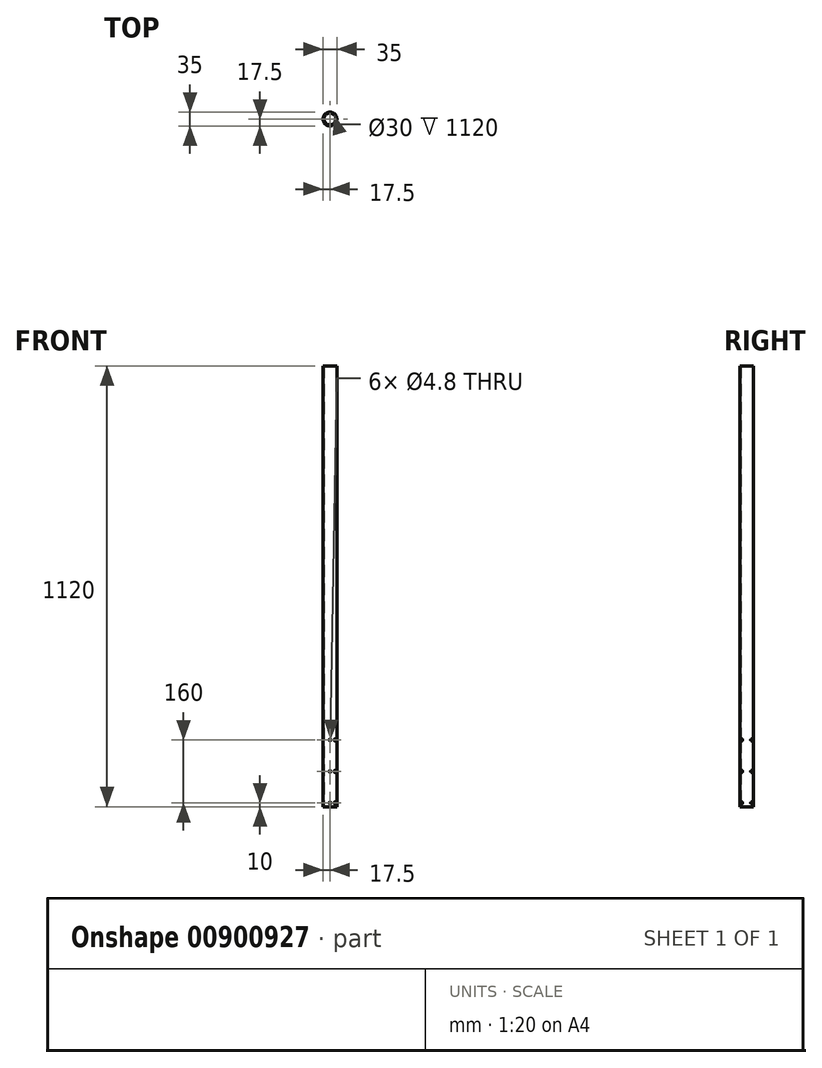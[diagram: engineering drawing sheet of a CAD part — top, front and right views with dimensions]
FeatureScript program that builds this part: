
annotation { "Feature Type Name" : "Feature", "Feature Type Description" : "" }
export const myFeature = defineFeature(function(context is Context, id is Id, definition is map)
    precondition{}
    {
        {
            var Q0;
            Q0=qCreatedBy(makeId("Top.planeOp"),FACE);
            var sketch = newSketch(context, id + "F0", { "sketchPlane" : qUnion([Q0])});
            skCircle(sketch, "E0", {"center": v(0, 0) * mm, "radius": 17.5 * mm});
            skLineSegment(sketch, "E1", {"start": v(0, 17.5) * mm, "end": v(0, -17.5) * mm});
            skSolve(sketch);
        }
        {
            var Q0;
            Q0 = qSketchRegion(id + "F0", true);
            extrude(context, id + "F1", {"entities" : qUnion([Q0]), "depth" : 1120 * mm, "offsetDistance" : 25 * mm});
        }
        {
            var Q0;
            Q0=sQuery(id+"F0.wireOp",VERTEX,"E0.center");
            var Q1;
            Q1=makeQuery(id+"F1.opExtrude","SWEPT_BODY",BODY,{"disambiguationData":[OSD([sQuery(id+"F0.wireOp",EDGE,"E0")])]});
            hole(context, id + "F2", {"style" : HoleStyle.SIMPLE, "endStyle" : HoleEndStyle.THROUGH, "oppositeDirection" : true, "holeDiameter" : 30 * mm, "majorDiameter" : 10 * mm, "isTappedThrough" : true, "tappedDepth" : 12 * mm, "tapClearance" : 3, "locations" : qUnion([Q0]), "scope" : qUnion([Q1])});
        }
        {
            var Q0;
            Q0=qCreatedBy(makeId("Front.planeOp"),FACE);
            var sketch = newSketch(context, id + "F3", { "sketchPlane" : qUnion([Q0])});
            skLineSegment(sketch, "E2.bottom", {"start": v(-17.5, 10) * mm, "end": v(17.5, 10) * mm});
            skLineSegment(sketch, "E2.top", {"start": v(-17.5, -10) * mm, "end": v(17.5, -10) * mm});
            skLineSegment(sketch, "E2.left", {"start": v(-17.5, 10) * mm, "end": v(-17.5, -10) * mm});
            skLineSegment(sketch, "E2.right", {"start": v(17.5, 10) * mm, "end": v(17.5, -10) * mm});
            skPoint(sketch, "E2.middle", {"position": v(0, 0) * mm});
            skLineSegment(sketch, "E3.top", {"start": v(-17.5, 90) * mm, "end": v(17.5, 90) * mm});
            skLineSegment(sketch, "E3.left", {"start": v(-17.5, 10) * mm, "end": v(-17.5, 90) * mm});
            skLineSegment(sketch, "E3.right", {"start": v(17.5, 10) * mm, "end": v(17.5, 90) * mm});
            skLineSegment(sketch, "E4.top", {"start": v(-17.5, 170) * mm, "end": v(17.5, 170) * mm});
            skLineSegment(sketch, "E4.left", {"start": v(-17.5, 90) * mm, "end": v(-17.5, 170) * mm});
            skLineSegment(sketch, "E4.right", {"start": v(17.5, 90) * mm, "end": v(17.5, 170) * mm});
            skLineSegment(sketch, "E5", {"start": v(-17.5, 170) * mm, "end": v(17.5, 10) * mm});
            skSolve(sketch);
        }
        {
            var Q0;
            Q0=qCreatedBy(makeId("Front.planeOp"),FACE);
            var sketch = newSketch(context, id + "F4", { "sketchPlane" : qUnion([Q0])});
            skCircle(sketch, "E6", {"center": v(0, 10) * mm, "radius": 2.4 * mm});
            skCircle(sketch, "E7", {"center": v(0, 90) * mm, "radius": 2.4 * mm});
            skCircle(sketch, "E8", {"center": v(0, 170) * mm, "radius": 2.4 * mm});
            skSolve(sketch);
        }
        {
            var Q0;
            Q0 = qSketchRegion(id + "F4", true);
            extrude(context, id + "F5", {"entities" : qUnion([Q0]), "operationType" : NewBodyOperationType.REMOVE, "endBound" : BoundingType.SYMMETRIC, "depth" : 50 * mm, "offsetDistance" : 25 * mm});
        }
        {
            var Q0;
            Q0=qCreatedBy(makeId("Front.planeOp"),FACE);
            var Q1;
            Q1=qCreatedBy(makeId("Right.planeOp"),FACE);
            cPlane(context, id + "F6", {"entities" : qUnion([Q0, Q1]), "cplaneType" : CPlaneType.MID_PLANE, "offset" : 25 * mm, "width" : 150 * mm, "height" : 150 * mm});
        }
        {
            var Q0;
            Q0=qCreatedBy(id+"F6.planeOp",FACE);
            var sketch = newSketch(context, id + "F7", { "sketchPlane" : qUnion([Q0])});
            skLineSegment(sketch, "E9.top", {"start": v(17.5, 10) * mm, "end": v(-17.5, 10) * mm});
            skPoint(sketch, "E9.middle", {"position": v(0, 0) * mm});
            skCircle(sketch, "E10", {"center": v(0, 170) * mm, "radius": 2.4 * mm});
            skCircle(sketch, "E11", {"center": v(0, 90) * mm, "radius": 2.4 * mm});
            skCircle(sketch, "E12", {"center": v(0, 10) * mm, "radius": 2.4 * mm});
            skSolve(sketch);
        }
        {
            var Q0;
            Q0 = qSketchRegion(id + "F7", true);
            extrude(context, id + "F8", {"entities" : qUnion([Q0]), "operationType" : NewBodyOperationType.REMOVE, "oppositeDirection" : true, "depth" : 35 * mm, "offsetDistance" : 25 * mm});
        }
        {
            var Q0;
            Q0=qCreatedBy(makeId("Right.planeOp"),FACE);
            var Q1;
            Q1=qCreatedBy(makeId("Front.planeOp"),FACE);
            cPlane(context, id + "F9", {"entities" : qUnion([Q0, Q1]), "cplaneType" : CPlaneType.MID_PLANE, "offset" : 25 * mm, "flipAlignment" : true, "width" : 150 * mm, "height" : 150 * mm});
        }
        {
            var Q0;
            Q0=qCreatedBy(id+"F9.planeOp",FACE);
            var sketch = newSketch(context, id + "F10", { "sketchPlane" : qUnion([Q0])});
            skLineSegment(sketch, "E13.top", {"start": v(2.4, 10) * mm, "end": v(-2.4, 10) * mm});
            skLineSegment(sketch, "E14.bottom", {"start": v(-2.4, 10) * mm, "end": v(2.4, 10) * mm});
            skLineSegment(sketch, "E15.bottom", {"start": v(-2.4, 90) * mm, "end": v(2.4, 90) * mm});
            skLineSegment(sketch, "E15.top", {"start": v(-2.4, 170) * mm, "end": v(2.4, 170) * mm});
            skLineSegment(sketch, "E16", {"start": v(-0.51, 92.34) * mm, "end": v(0.51, 87.66) * mm});
            skCircle(sketch, "E17", {"center": v(0, 170) * mm, "radius": 2.4 * mm});
            skCircle(sketch, "E18", {"center": v(0, 90) * mm, "radius": 2.4 * mm});
            skCircle(sketch, "E19", {"center": v(0, 10) * mm, "radius": 2.4 * mm});
            skSolve(sketch);
        }
        {
            var Q0;
            Q0 = qSketchRegion(id + "F10", true);
            extrude(context, id + "F11", {"entities" : qUnion([Q0]), "operationType" : NewBodyOperationType.REMOVE, "depth" : 18 * mm, "offsetDistance" : 25 * mm});
        }
    });
